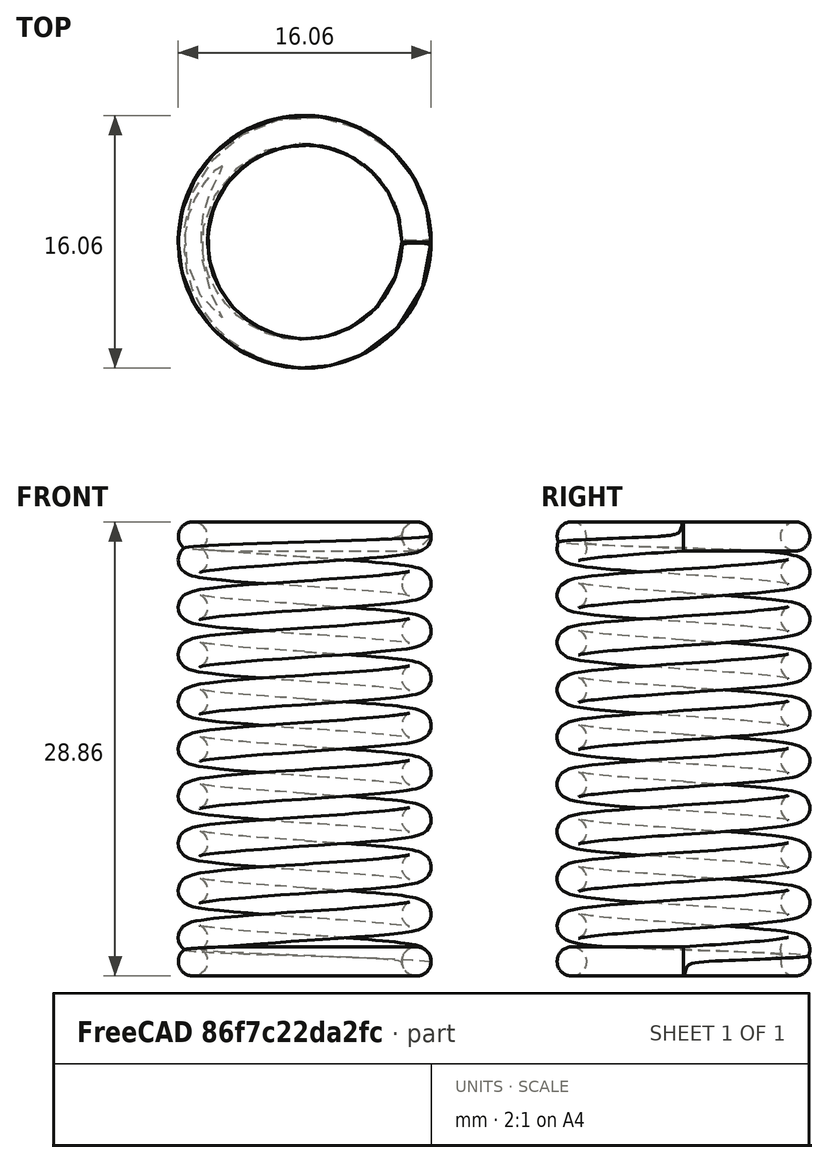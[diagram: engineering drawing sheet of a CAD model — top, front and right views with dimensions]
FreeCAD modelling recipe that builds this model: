
FCSTD DOCUMENT  (FreeCAD 0.16R5919 (Git))
Label: ressort
License: CreativeCommons Attribution
LicenseURL: http://creativecommons.org/licenses/by/4.0/
objects: Part::MultiFuse×2, Part::Helix×1, Part::Circle×1, Part::Sweep×1, Part::Torus×1, Part::FeaturePython×1
note: 7 computed .brp shape members not serialized (recipe doc carries the construction recipe); baked Part::Feature solids carry a one-line shape summary decoded from their .brp

FEATURE [Part::Helix] Helix  label="Hélice"
  Angle = 0
  Height = 27
  LocalCoord = 0
  Pitch = 3
  Radius = 7.1
  Style = 1
FEATURE [Part::Circle] Circle  label="Cercle"
  Angle0 = 0
  Angle1 = 360
  Placement = pos=(7.1,0,0) rot=(-0.57735,-0.57735,-0.57735;2.0944rad)
  Radius = 0.93
FEATURE [Part::Sweep] Sweep
  Frenet = true
  Sections = -> [Circle]
  Solid = true
  Spine = -> Helix [Edge1,Edge2,Edge3,Edge4,Edge5,Edge6,Edge7,Edge8,Edge9]
  Transition = 1
FEATURE [Part::Torus] Torus  label="Tore"
  Angle1 = -180
  Angle2 = 180
  Angle3 = 360
  Radius1 = 7.1
  Radius2 = 0.925
FEATURE [Part::FeaturePython] Clone  label="Clone of Tore"  # Draft clone (typed FeaturePython)
  Objects = -> [Torus]
  Placement = pos=(0,0,27) rot=(0,0,1;0rad)
  Scale = (1,1,1)
FEATURE [Part::MultiFuse] Fusion
  Shapes = -> [Sweep,Torus]
FEATURE [Part::MultiFuse] Fusion001
  Shapes = -> [Clone,Fusion]
